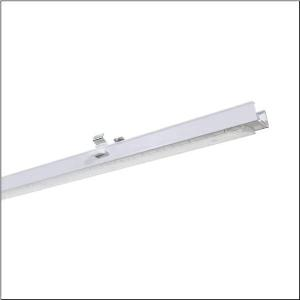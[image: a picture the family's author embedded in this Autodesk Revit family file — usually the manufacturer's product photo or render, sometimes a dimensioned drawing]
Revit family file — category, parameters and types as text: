
# Revit family: trunking_flex_31_51re18mb1cb
name_source: partatom
category: Lighting Fixtures
units: mm (PartAtom-declared; Revit-internal decimal feet)

## family parameters
Cut with Voids When Loaded = No
Host = Face
Light Source = No
Part Type = Normal
Room Calculation Point = No
Round Connector Dimension = Use Diameter
Shared = No

## types (1)
- --- (1 x LED, 11500 lm, 66 W, 3500K)
    Apparent Load = 66 VA
    CIE Flux Codes = 71 89 97 97 100
    Color Rendering = 80
    Color Temperature = 3500K
    Default Elevation = 1800 mm
    Description = Trunking Flex 31, luminaire insert, of extruded aluminium section, coated, traffic white (RAL 9016), length: 1.472mm, width: 91mm, height: 53mm, LED rated luminous flux: 11.500lm, light colour: 835, control gear: ON/OFF Multilumen, with system connector: socket, mains connection: 220..240V, AC, 50/60Hz, rated input power: 66W, luminous flux adjustable on luminaire in eight steps (3450/4380/5800/6700/8350/9200/10500/11500lm ), connected load according to luminous flux setting (19/24/32/37/47/52/60/66W), primary light control with lens, of plastic, primary optical cover: cover, of PMMA, light emission: direct distribution, protection rating (complete): IP20, insulation class (complete): insulation class I (protective earthing), certification: CE, UKCA, impact resistance: IK02, permissible ambient temperature for indoor applications: -20..+40°C, packaging unit: 1 piece
    Height = 58 mm
    Lamp = 1 x LED
    Lamp Light Flux = 11500 lm
    Lamp Power = 66 W
    Lamp count = 1
    Length = 1472 mm
    Luminous efficacy = 174 lm/W
    Manufacturer = Siteco
    ModVariant = No
    Model = 51RE18MB1CB
    Mounting Place = Ceiling
    Mounting Type = Pendant
    Number of Poles = 1
    OnlyDefault = Yes
    Power Factor = 1
    Product Name = Trunking Flex 31
    Product group = luminaire insert
    ProductGroupID = 901
    Protection Class = Protection class I
    Protection Degree = IP 20
    RLX_Detail_Level = 1
    RLX_Emergency_Light_Flux = 0 lm
    RLX_Emergency_Type = 0
    RLX_Emergency_Type_DB = No
    RlxData = <blob elided: 21117 chars, md5=d28d3719>
    Socket = socket
    Standby Power = 0 W
    System Light Flux = 11500 lm
    System Power = 66 W
    Type Comments = factory setting: luminous flux: 100 % | (ON | ON | ON)
    Type Image = l_1266702.jpg
    URL = http://relux.com
    VarID = @adj_001201
    Voltage = 0 V
    Weight = 0.00 kg
    Width = 65 mm

## geometry (parser evidence)
native form markers: Blend x4, Sweep x13
no freeform markers — native parametric forms only
